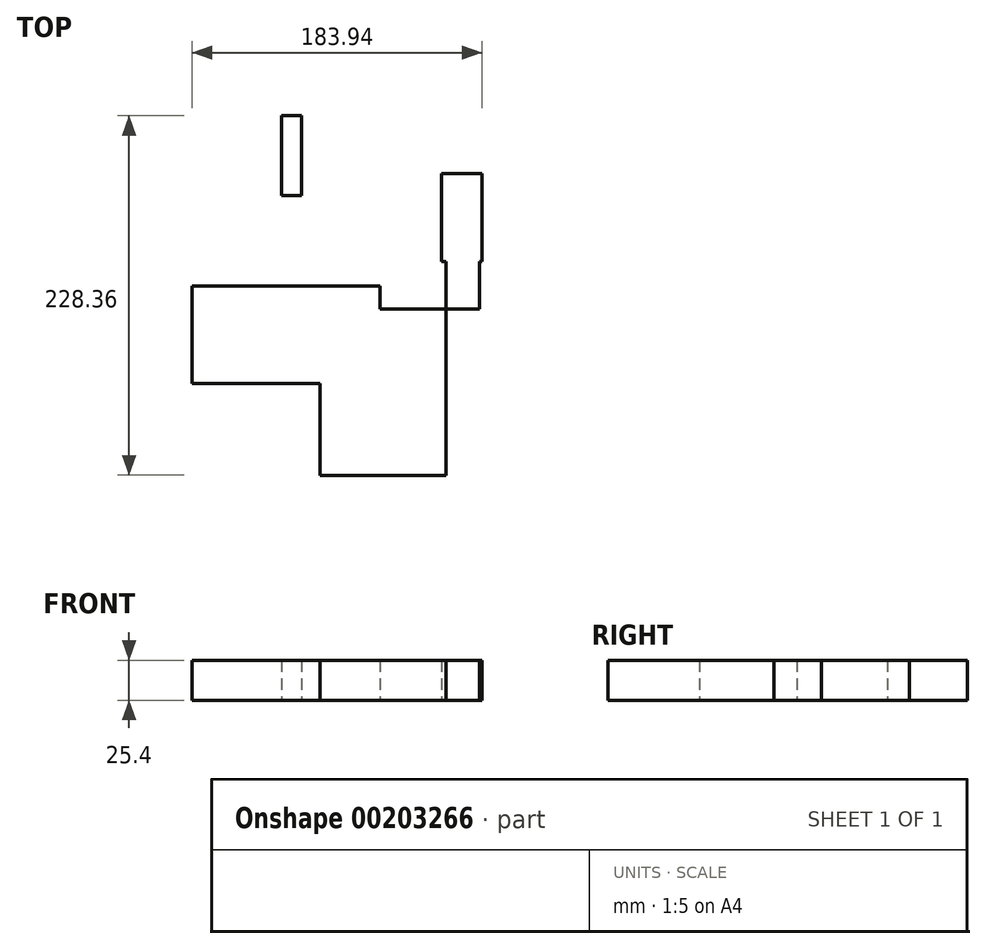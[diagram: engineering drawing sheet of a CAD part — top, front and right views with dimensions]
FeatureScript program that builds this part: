
annotation { "Feature Type Name" : "Feature", "Feature Type Description" : "" }
export const myFeature = defineFeature(function(context is Context, id is Id, definition is map)
    precondition{}
    {
        {
            var Q0;
            Q0=qCreatedBy(makeId("Top.planeOp"),FACE);
            var sketch = newSketch(context, id + "F0", { "sketchPlane" : qUnion([Q0])});
            skLineSegment(sketch, "E0.bottom", {"start": v(3.55, 0) * mm, "end": v(-115.64, 0) * mm});
            skLineSegment(sketch, "E0.top", {"start": v(3.55, -61.74) * mm, "end": v(-115.64, -61.74) * mm});
            skLineSegment(sketch, "E0.left", {"start": v(3.55, 0) * mm, "end": v(3.55, -61.74) * mm});
            skLineSegment(sketch, "E0.right", {"start": v(-115.64, 0) * mm, "end": v(-115.64, -61.74) * mm});
            skLineSegment(sketch, "E1.bottom", {"start": v(-58.75, 57.45) * mm, "end": v(-46.05, 57.45) * mm});
            skLineSegment(sketch, "E1.top", {"start": v(-58.75, 108.25) * mm, "end": v(-46.05, 108.25) * mm});
            skLineSegment(sketch, "E1.left", {"start": v(-58.75, 57.45) * mm, "end": v(-58.75, 108.25) * mm});
            skLineSegment(sketch, "E1.right", {"start": v(-46.05, 57.45) * mm, "end": v(-46.05, 108.25) * mm});
            skLineSegment(sketch, "E2.bottom", {"start": v(42.85, 71.42) * mm, "end": v(68.3, 71.42) * mm});
            skLineSegment(sketch, "E2.top", {"start": v(42.85, 15.67) * mm, "end": v(68.3, 15.67) * mm});
            skLineSegment(sketch, "E2.left", {"start": v(42.85, 71.42) * mm, "end": v(42.85, 15.67) * mm});
            skLineSegment(sketch, "E2.right", {"start": v(68.3, 71.42) * mm, "end": v(68.3, 15.67) * mm});
            skLineSegment(sketch, "E3.bottom", {"start": v(66.71, 15.93) * mm, "end": v(45.7, 15.93) * mm});
            skLineSegment(sketch, "E3.top", {"start": v(66.71, -14.4) * mm, "end": v(45.7, -14.4) * mm});
            skLineSegment(sketch, "E3.left", {"start": v(66.71, 15.93) * mm, "end": v(66.71, -14.4) * mm});
            skLineSegment(sketch, "E3.right", {"start": v(45.7, 15.93) * mm, "end": v(45.7, -14.4) * mm});
            skLineSegment(sketch, "E4.bottom", {"start": v(45.7, -14.4) * mm, "end": v(-34.34, -14.4) * mm});
            skLineSegment(sketch, "E4.top", {"start": v(45.7, -120.11) * mm, "end": v(-34.34, -120.11) * mm});
            skLineSegment(sketch, "E4.left", {"start": v(45.7, -14.4) * mm, "end": v(45.7, -120.11) * mm});
            skLineSegment(sketch, "E4.right", {"start": v(-34.34, -14.4) * mm, "end": v(-34.34, -120.11) * mm});
            skSolve(sketch);
        }
        {
            var Q0;
            Q0 = qSketchRegion(id + "F0", true);
            extrude(context, id + "F1", {"entities" : qUnion([Q0]), "depth" : 25.4 * mm});
        }
    });
